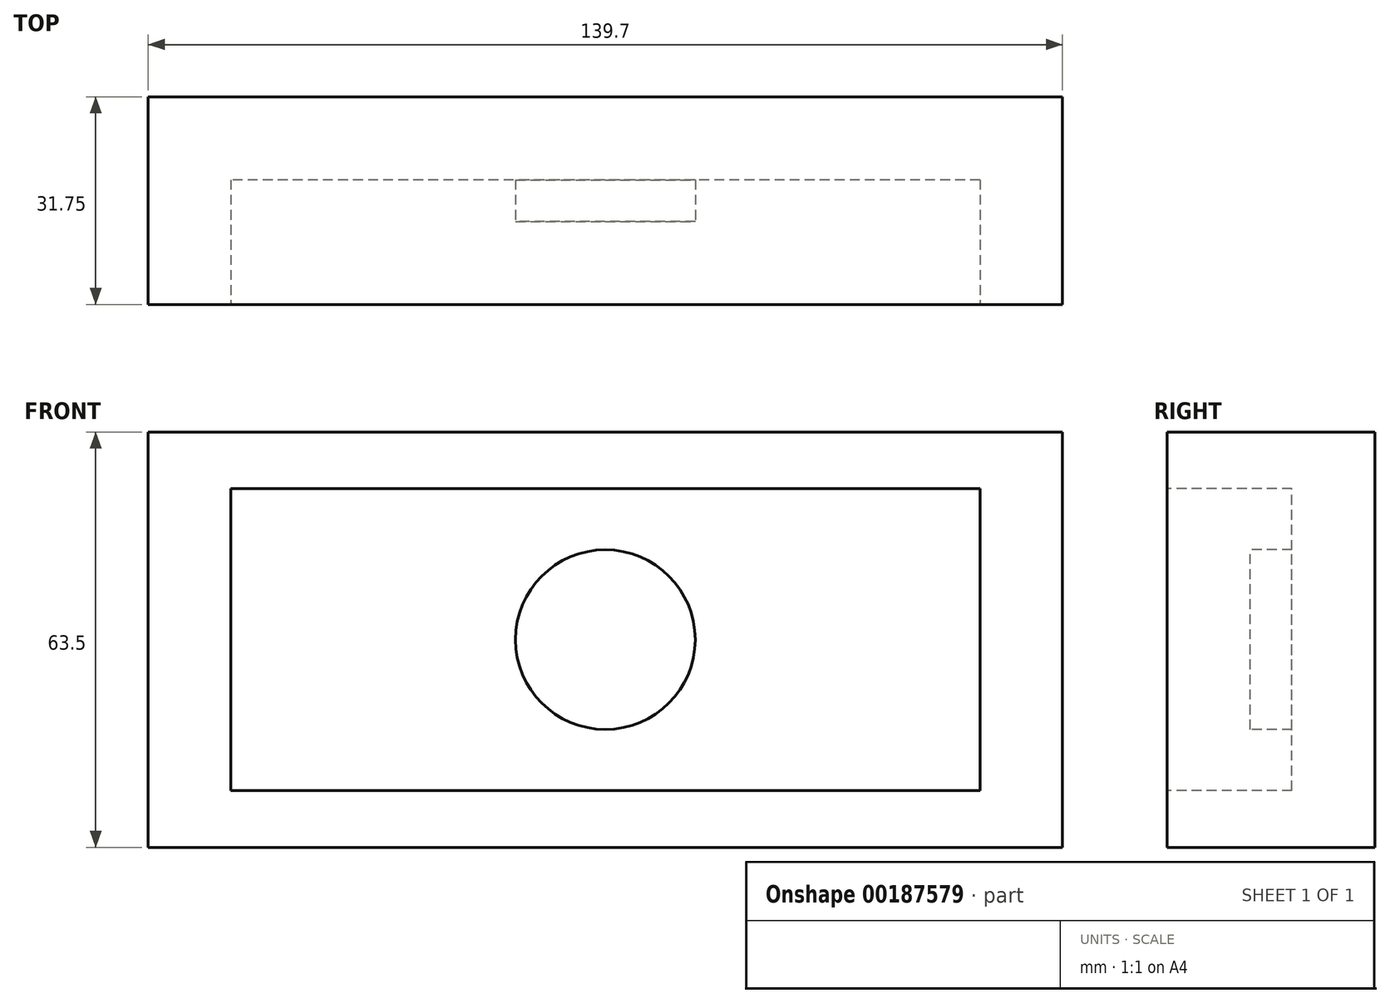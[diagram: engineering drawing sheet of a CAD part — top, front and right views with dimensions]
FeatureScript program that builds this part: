
annotation { "Feature Type Name" : "Feature", "Feature Type Description" : "" }
export const myFeature = defineFeature(function(context is Context, id is Id, definition is map)
    precondition{}
    {
        {
            var Q0;
            Q0=qCreatedBy(makeId("Front.planeOp"),FACE);
            var sketch = newSketch(context, id + "F0", { "sketchPlane" : qUnion([Q0])});
            skLineSegment(sketch, "E0.bottom", {"start": v(69.85, -31.75) * mm, "end": v(-69.85, -31.75) * mm});
            skLineSegment(sketch, "E0.top", {"start": v(69.85, 31.75) * mm, "end": v(-69.85, 31.75) * mm});
            skLineSegment(sketch, "E0.left", {"start": v(69.85, -31.75) * mm, "end": v(69.85, 31.75) * mm});
            skLineSegment(sketch, "E0.right", {"start": v(-69.85, -31.75) * mm, "end": v(-69.85, 31.75) * mm});
            skPoint(sketch, "E0.middle", {"position": v(0, 0) * mm});
            skSolve(sketch);
        }
        {
            var Q0;
            Q0=makeQuery(id+"F0.imprint","IMPRINT",FACE,{"disambiguationData":[TD([[makeQuery(id+"F0.imprint","IMPRINT",EDGE,{"derivedFrom":sQuery(id+"F0.wireOp",EDGE,"E0.bottom")}),-1.0]])]});
            extrude(context, id + "F1", {"entities" : qUnion([Q0]), "depth" : 31.75 * mm});
        }
        {
            var Q0;
            Q0=makeQuery(id+"F1.opExtrude","CAP_FACE",FACE,{"disambiguationData":[OSD([sQuery(id+"F0.wireOp",EDGE,"E0.bottom"),sQuery(id+"F0.wireOp",EDGE,"E0.top"),sQuery(id+"F0.wireOp",EDGE,"E0.left"),sQuery(id+"F0.wireOp",EDGE,"E0.right")])],"isStart":false});
            var sketch = newSketch(context, id + "F2", { "sketchPlane" : qUnion([Q0])});
            skLineSegment(sketch, "E1.bottom", {"start": v(57.26, -23.06) * mm, "end": v(-57.26, -23.06) * mm});
            skLineSegment(sketch, "E1.top", {"start": v(57.26, 23.06) * mm, "end": v(-57.26, 23.06) * mm});
            skLineSegment(sketch, "E1.left", {"start": v(57.26, -23.06) * mm, "end": v(57.26, 23.06) * mm});
            skLineSegment(sketch, "E1.right", {"start": v(-57.26, -23.06) * mm, "end": v(-57.26, 23.06) * mm});
            skPoint(sketch, "E1.middle", {"position": v(0, 0) * mm});
            skSolve(sketch);
        }
        {
            var Q0;
            Q0=makeQuery(id+"F2.imprint","IMPRINT",FACE,{"disambiguationData":[TD([[makeQuery(id+"F2.imprint","IMPRINT",EDGE,{"derivedFrom":sQuery(id+"F2.wireOp",EDGE,"E1.bottom")}),-1.0]])]});
            extrude(context, id + "F3", {"entities" : qUnion([Q0]), "operationType" : NewBodyOperationType.REMOVE, "oppositeDirection" : true, "depth" : 12.7 * mm});
        }
        {
            var Q0;
            Q0=makeQuery(id+"F3.boolean.opBoolean","COPY",FACE,{"derivedFrom":makeQuery(id+"F3.opExtrude","CAP_FACE",FACE,{"disambiguationData":[OSD([sQuery(id+"F2.wireOp",EDGE,"E1.bottom"),sQuery(id+"F2.wireOp",EDGE,"E1.top"),sQuery(id+"F2.wireOp",EDGE,"E1.left"),sQuery(id+"F2.wireOp",EDGE,"E1.right")])],"isStart":false})});
            var sketch = newSketch(context, id + "F4", { "sketchPlane" : qUnion([Q0])});
            skCircle(sketch, "E2", {"center": v(0, 0) * mm, "radius": 13.73 * mm});
            skSolve(sketch);
        }
        {
            var Q0;
            Q0=makeQuery(id+"F4.imprint","IMPRINT",FACE,{"disambiguationData":[TD([[makeQuery(id+"F4.imprint","IMPRINT",EDGE,{"derivedFrom":sQuery(id+"F4.wireOp",EDGE,"E2")}),-1.0]])]});
            extrude(context, id + "F5", {"entities" : qUnion([Q0]), "operationType" : NewBodyOperationType.REMOVE, "oppositeDirection" : true, "depth" : 6.35 * mm});
        }
    });
